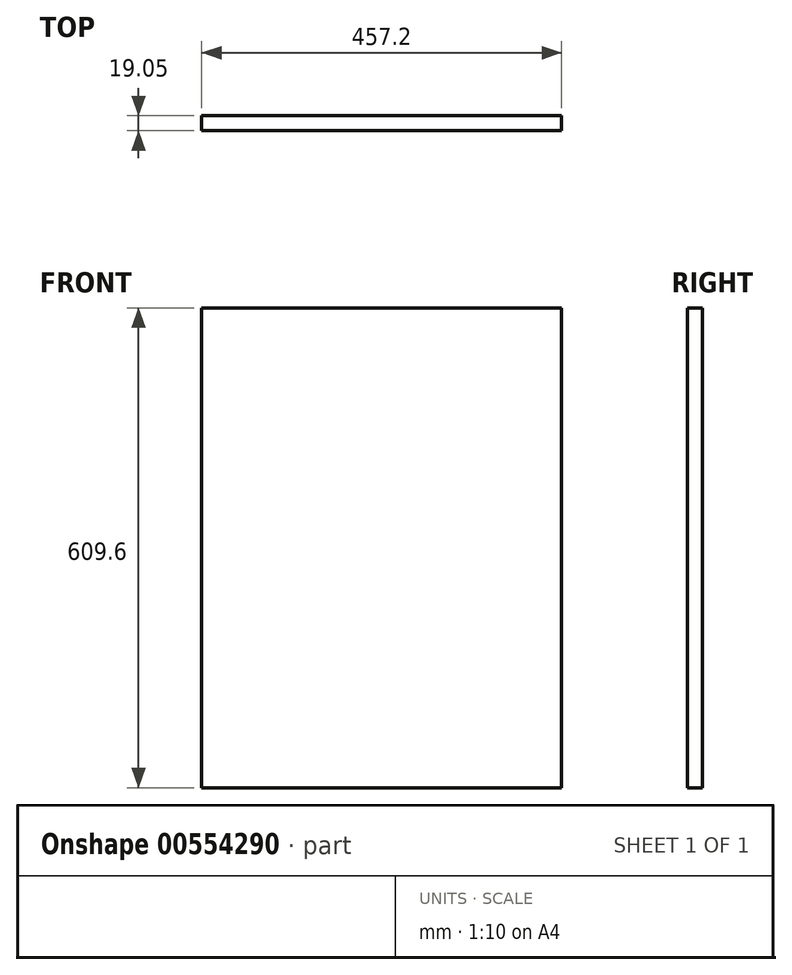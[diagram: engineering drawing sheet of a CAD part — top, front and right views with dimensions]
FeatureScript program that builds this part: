
annotation { "Feature Type Name" : "Feature", "Feature Type Description" : "" }
export const myFeature = defineFeature(function(context is Context, id is Id, definition is map)
    precondition{}
    {
        {
            var Q0;
            Q0=qCreatedBy(makeId("Front.planeOp"),FACE);
            var sketch = newSketch(context, id + "F0", { "sketchPlane" : qUnion([Q0])});
            skLineSegment(sketch, "E0.bottom", {"start": v(-224.34, 387.86) * mm, "end": v(232.86, 387.86) * mm});
            skLineSegment(sketch, "E0.top", {"start": v(-224.34, -221.74) * mm, "end": v(232.86, -221.74) * mm});
            skLineSegment(sketch, "E0.left", {"start": v(-224.34, 387.86) * mm, "end": v(-224.34, -221.74) * mm});
            skLineSegment(sketch, "E0.right", {"start": v(232.86, 387.86) * mm, "end": v(232.86, -221.74) * mm});
            skSolve(sketch);
        }
        {
            var Q0;
            Q0=makeQuery(id+"F0.imprint","IMPRINT",FACE,{"disambiguationData":[TD([[makeQuery(id+"F0.imprint","IMPRINT",EDGE,{"derivedFrom":sQuery(id+"F0.wireOp",EDGE,"E0.bottom")}),-1.0]])]});
            extrude(context, id + "F1", {"entities" : qUnion([Q0]), "depth" : 19.05 * mm, "offsetDistance" : 25.4 * mm});
        }
    });
